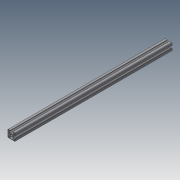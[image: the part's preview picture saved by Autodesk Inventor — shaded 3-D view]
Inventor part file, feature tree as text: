
AUTODESK INVENTOR PART (.ipt)
format: ipt  version: 2020.3 (Build 243373000, 373)  size: 303,616 bytes
history: native  units: in
note: dims shown in document units (in); Inventor stores cm internally (conversion verified against a paired STEP export)
features: extrude x1, sketch x1, projected_geometry x1, other x1
ambient origin geometry x8: Origin, YZ Plane, XZ Plane, XY Plane, X Axis, Y Axis, Z Axis, Center Point
bodies: Solid1 (feature_tree)
feature tree (4):
  extrude  "Extrusion1"  [1 undecoded]
  sketch  "Sketch1"  dims[d0=24.8031in d1=0.0in]
  projected_geometry  "Projected Loop1"
  other  "Boss-Extrude1"
note: 1 required parameter value undecoded (feature->parameter linkage not recoverable at this tier; creation-order binding heuristic only, values carry confidence <= 0.55)
